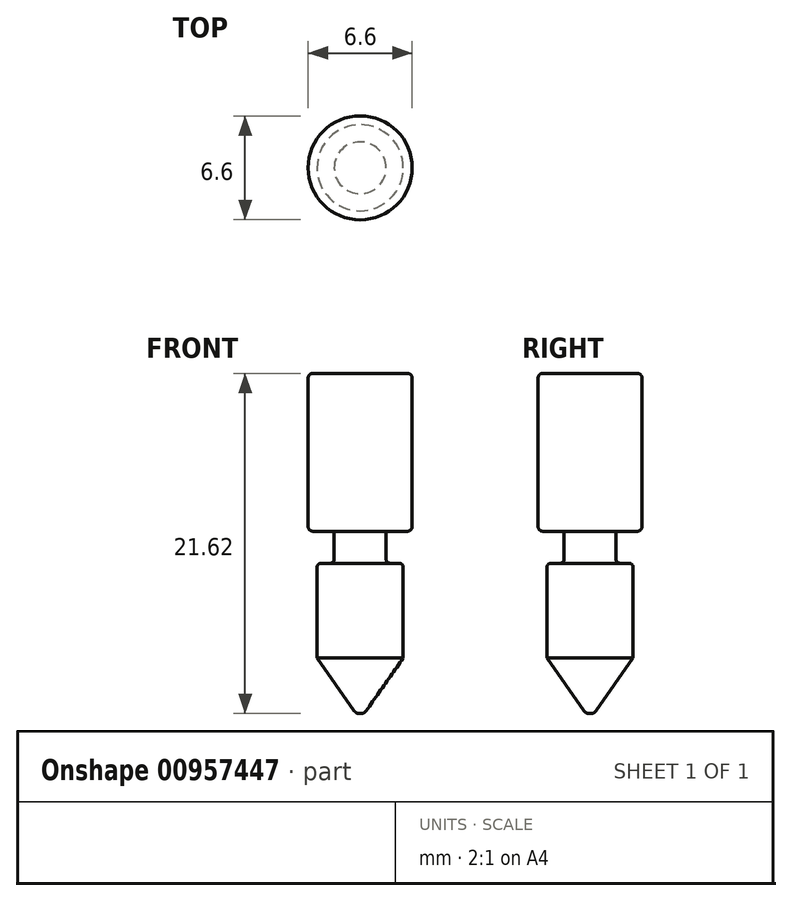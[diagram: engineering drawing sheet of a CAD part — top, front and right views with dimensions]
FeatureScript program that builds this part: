
annotation { "Feature Type Name" : "Feature", "Feature Type Description" : "" }
export const myFeature = defineFeature(function(context is Context, id is Id, definition is map)
    precondition{}
    {
        {
            var Q0;
            Q0=qCreatedBy(makeId("Front.planeOp"),FACE);
            var sketch = newSketch(context, id + "F0", { "sketchPlane" : qUnion([Q0])});
            skLineSegment(sketch, "E0", {"start": v(0.6, 21.62) * mm, "end": v(3.9, 21.62) * mm});
            skLineSegment(sketch, "E1", {"start": v(3.9, 21.62) * mm, "end": v(3.9, 11.58) * mm});
            skLineSegment(sketch, "E2", {"start": v(0.6, 0) * mm, "end": v(0.85, 0) * mm});
            skLineSegment(sketch, "E3.left", {"start": v(2.25, 11.58) * mm, "end": v(2.25, 9.55) * mm});
            skLineSegment(sketch, "E4", {"start": v(3.9, 11.58) * mm, "end": v(2.25, 11.58) * mm});
            skLineSegment(sketch, "E5", {"start": v(0.6, 21.62) * mm, "end": v(0.6, 0) * mm});
            skLineSegment(sketch, "E6", {"start": v(2.25, 9.55) * mm, "end": v(3.33, 9.55) * mm});
            skLineSegment(sketch, "E7", {"start": v(3.33, 9.55) * mm, "end": v(3.33, 3.53) * mm});
            skLineSegment(sketch, "E8", {"start": v(3.33, 3.53) * mm, "end": v(0.85, 0) * mm});
            skSolve(sketch);
        }
        {
            var Q0;
            Q0=makeQuery(id+"F0.imprint","IMPRINT",FACE,{"disambiguationData":[TD([[makeQuery(id+"F0.imprint","IMPRINT",EDGE,{"derivedFrom":sQuery(id+"F0.wireOp",EDGE,"E0")}),-1.0]])]});
            var Q1;
            Q1=sQuery(id+"F0.wireOp",EDGE,"E5");
            revolve(context, id + "F1", {"surfaceOperationType" : NewSurfaceOperationType.NEW, "entities" : qUnion([Q0]), "axis" : qUnion([Q1]), "revolveType" : RevolveType.FULL});
        }
        {
            var Q0;
            Q0=makeQuery(id+"F1.opRevolve","SWEPT_EDGE",EDGE,{"disambiguationData":[OSD([sQuery(id+"F0.wireOp",EDGE,"E0"),sQuery(id+"F0.wireOp",EDGE,"E1")])]});
            var Q1;
            Q1=makeQuery(id+"F1.opRevolve","SWEPT_EDGE",EDGE,{"disambiguationData":[OSD([sQuery(id+"F0.wireOp",EDGE,"nacutCgs-iXgb-V6nK-TU8P-15SqQ78KMzG6"),sQuery(id+"F0.wireOp",EDGE,"PXFEtYn9-CnmJ-ErxW-mMbQ-JwHdpA7ZR6Q8")])]});
            var Q2;
            Q2=makeQuery(id+"F1.opRevolve","SWEPT_EDGE",EDGE,{"disambiguationData":[OSD([sQuery(id+"F0.wireOp",EDGE,"PXFEtYn9-CnmJ-ErxW-mMbQ-JwHdpA7ZR6Q8"),sQuery(id+"F0.wireOp",EDGE,"mtS6X4IM-4P4w-L51a-iSDW-R0GdbDv5Fx9C")])]});
            var Q3;
            Q3=makeQuery(id+"F1.opRevolve","SWEPT_EDGE",EDGE,{"disambiguationData":[OSD([sQuery(id+"F0.wireOp",EDGE,"E1"),sQuery(id+"F0.wireOp",EDGE,"GaB8lm0x-aMqK-8snU-kis9-f1ezWCm4xxv6")])]});
            fillet(context, id + "F2", {"entities" : qUnion([Q0, Q1, Q2, Q3]), "radius" : 0.3 * mm, "tangentPropagation" : true, "allowEdgeOverflow" : false});
        }
        {
            var Q0;
            Q0=makeQuery(id+"F1.opRevolve","SWEPT_FACE",FACE,{"disambiguationData":[OSD([sQuery(id+"F0.wireOp",EDGE,"E2")])]});
            fillet(context, id + "F3", {"entities" : qUnion([Q0]), "radius" : 0.43 * mm, "tangentPropagation" : true, "allowEdgeOverflow" : false});
        }
        {
            var Q0;
            Q0=makeQuery(id+"F1.opRevolve","SWEPT_FACE",FACE,{"disambiguationData":[OSD([sQuery(id+"F0.wireOp",EDGE,"E6")])]});
            fillet(context, id + "F4", {"entities" : qUnion([Q0]), "radius" : 0.25 * mm, "tangentPropagation" : true, "allowEdgeOverflow" : false});
        }
    });
